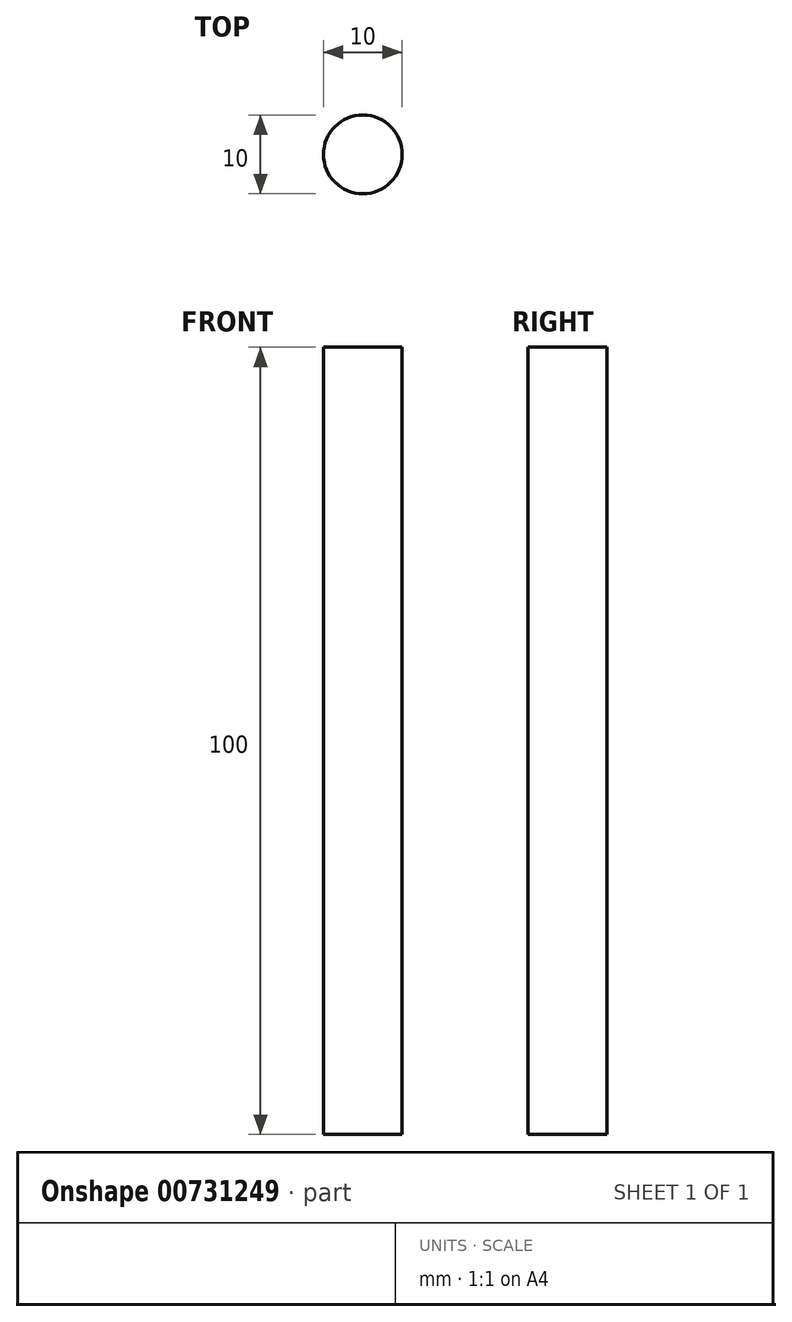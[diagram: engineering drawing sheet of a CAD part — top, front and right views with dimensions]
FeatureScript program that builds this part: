
annotation { "Feature Type Name" : "Feature", "Feature Type Description" : "" }
export const myFeature = defineFeature(function(context is Context, id is Id, definition is map)
    precondition{}
    {
        {
            var Q0;
            Q0=qCreatedBy(makeId("Top.planeOp"),FACE);
            var sketch = newSketch(context, id + "F0", { "sketchPlane" : qUnion([Q0])});
            skCircle(sketch, "E0", {"center": v(0, 0) * mm, "radius": 5 * mm});
            skSolve(sketch);
        }
        {
            var Q0;
            Q0 = qSketchRegion(id + "F0", true);
            extrude(context, id + "F1", {"entities" : qUnion([Q0]), "depth" : 100 * mm, "offsetDistance" : 25.4 * mm});
        }
    });
